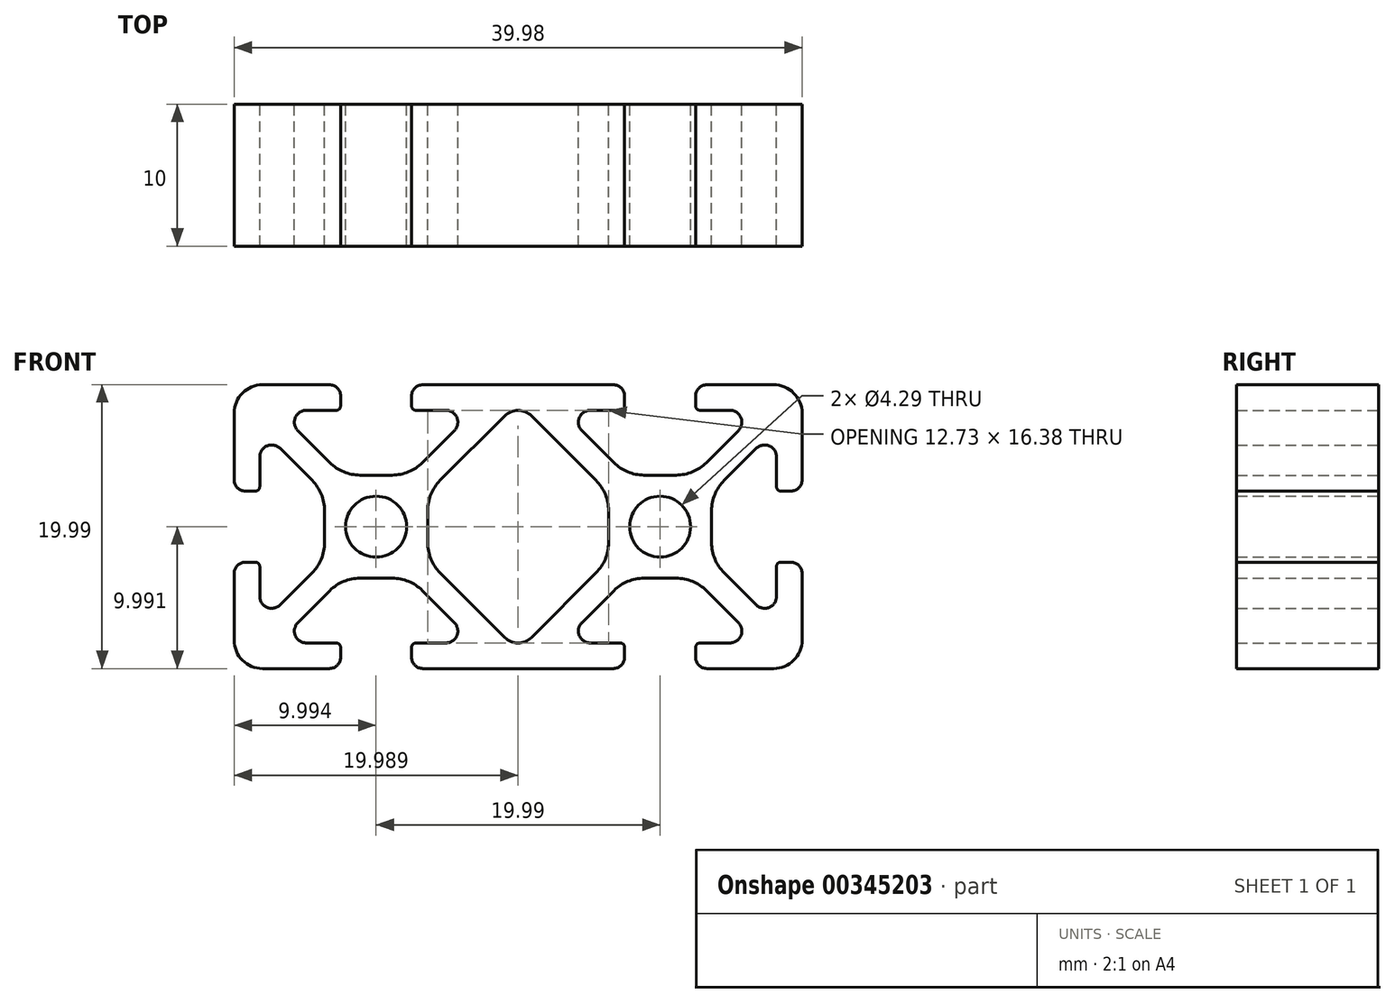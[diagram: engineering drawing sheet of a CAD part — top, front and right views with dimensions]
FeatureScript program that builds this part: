
annotation { "Feature Type Name" : "Feature", "Feature Type Description" : "" }
export const myFeature = defineFeature(function(context is Context, id is Id, definition is map)
    precondition{}
    {
        {
            var Q0;
            Q0=qCreatedBy(makeId("Front.planeOp"),FACE);
            var sketch = newSketch(context, id + "F0", { "sketchPlane" : qUnion([Q0])});
            skArc(sketch, "E0.0.0", {"start": v(-12.02, 4.76) * mm, "mid": v(-13.17, 4.99) * mm, "end": v(-14.14, 5.64) * mm});
            skLineSegment(sketch, "E0.0.1", {"start": v(-14.14, 5.64) * mm, "end": v(-16.4, 7.9) * mm});
            skArc(sketch, "E0.0.2", {"start": v(-16.4, 7.9) * mm, "mid": v(-16.58, 8.8) * mm, "end": v(-15.8, 9.32) * mm});
            skLineSegment(sketch, "E0.0.3", {"start": v(-15.8, 9.32) * mm, "end": v(-13.7, 9.32) * mm});
            skArc(sketch, "E0.0.4", {"start": v(-13.7, 9.32) * mm, "mid": v(-13.48, 9.41) * mm, "end": v(-13.39, 9.63) * mm});
            skLineSegment(sketch, "E0.0.5", {"start": v(-13.39, 9.63) * mm, "end": v(-13.39, 10.34) * mm});
            skArc(sketch, "E0.0.6", {"start": v(-13.39, 10.34) * mm, "mid": v(-13.62, 10.9) * mm, "end": v(-14.18, 11.13) * mm});
            skLineSegment(sketch, "E0.0.7", {"start": v(-14.18, 11.13) * mm, "end": v(-18.87, 11.13) * mm});
            skArc(sketch, "E0.0.8", {"start": v(-18.87, 11.13) * mm, "mid": v(-20.3, 10.54) * mm, "end": v(-20.88, 9.12) * mm});
            skLineSegment(sketch, "E0.0.9", {"start": v(-20.88, 9.12) * mm, "end": v(-20.88, 4.42) * mm});
            skArc(sketch, "E0.0.10", {"start": v(-20.88, 4.42) * mm, "mid": v(-20.65, 3.86) * mm, "end": v(-20.1, 3.63) * mm});
            skLineSegment(sketch, "E0.0.11", {"start": v(-20.1, 3.63) * mm, "end": v(-19.38, 3.63) * mm});
            skArc(sketch, "E0.0.12", {"start": v(-19.38, 3.63) * mm, "mid": v(-19.17, 3.72) * mm, "end": v(-19.08, 3.94) * mm});
            skLineSegment(sketch, "E0.0.13", {"start": v(-19.08, 3.94) * mm, "end": v(-19.08, 6.05) * mm});
            skArc(sketch, "E0.0.14", {"start": v(-19.08, 6.05) * mm, "mid": v(-18.56, 6.82) * mm, "end": v(-17.65, 6.64) * mm});
            skLineSegment(sketch, "E0.0.15", {"start": v(-17.65, 6.64) * mm, "end": v(-15.4, 4.38) * mm});
            skArc(sketch, "E0.0.16", {"start": v(-15.4, 4.38) * mm, "mid": v(-14.74, 3.41) * mm, "end": v(-14.51, 2.26) * mm});
            skLineSegment(sketch, "E0.0.17", {"start": v(-14.51, 2.26) * mm, "end": v(-14.51, 0) * mm});
            skArc(sketch, "E0.0.18", {"start": v(-14.51, 0) * mm, "mid": v(-14.74, -1.15) * mm, "end": v(-15.4, -2.12) * mm});
            skLineSegment(sketch, "E0.0.19", {"start": v(-15.4, -2.12) * mm, "end": v(-17.65, -4.38) * mm});
            skArc(sketch, "E0.0.20", {"start": v(-17.65, -4.38) * mm, "mid": v(-18.56, -4.56) * mm, "end": v(-19.08, -3.78) * mm});
            skLineSegment(sketch, "E0.0.21", {"start": v(-19.08, -3.78) * mm, "end": v(-19.08, -1.68) * mm});
            skArc(sketch, "E0.0.22", {"start": v(-19.08, -1.68) * mm, "mid": v(-19.17, -1.46) * mm, "end": v(-19.38, -1.37) * mm});
            skLineSegment(sketch, "E0.0.23", {"start": v(-19.38, -1.37) * mm, "end": v(-20.1, -1.37) * mm});
            skArc(sketch, "E0.0.24", {"start": v(-20.1, -1.37) * mm, "mid": v(-20.65, -1.6) * mm, "end": v(-20.88, -2.16) * mm});
            skLineSegment(sketch, "E0.0.25", {"start": v(-20.88, -2.16) * mm, "end": v(-20.88, -6.86) * mm});
            skArc(sketch, "E0.0.26", {"start": v(-20.88, -6.86) * mm, "mid": v(-20.3, -8.28) * mm, "end": v(-18.87, -8.86) * mm});
            skLineSegment(sketch, "E0.0.27", {"start": v(-18.87, -8.86) * mm, "end": v(-14.18, -8.86) * mm});
            skArc(sketch, "E0.0.28", {"start": v(-14.18, -8.86) * mm, "mid": v(-13.62, -8.63) * mm, "end": v(-13.39, -8.08) * mm});
            skLineSegment(sketch, "E0.0.29", {"start": v(-13.39, -8.08) * mm, "end": v(-13.39, -7.36) * mm});
            skArc(sketch, "E0.0.30", {"start": v(-13.39, -7.36) * mm, "mid": v(-13.48, -7.15) * mm, "end": v(-13.7, -7.06) * mm});
            skLineSegment(sketch, "E0.0.31", {"start": v(-13.7, -7.06) * mm, "end": v(-15.8, -7.06) * mm});
            skArc(sketch, "E0.0.32", {"start": v(-15.8, -7.06) * mm, "mid": v(-16.58, -6.54) * mm, "end": v(-16.4, -5.63) * mm});
            skLineSegment(sketch, "E0.0.33", {"start": v(-16.4, -5.63) * mm, "end": v(-14.14, -3.37) * mm});
            skArc(sketch, "E0.0.34", {"start": v(-14.14, -3.37) * mm, "mid": v(-13.17, -2.72) * mm, "end": v(-12.02, -2.5) * mm});
            skLineSegment(sketch, "E0.0.35", {"start": v(-12.02, -2.5) * mm, "end": v(-9.75, -2.5) * mm});
            skArc(sketch, "E0.0.36", {"start": v(-9.75, -2.5) * mm, "mid": v(-8.6, -2.72) * mm, "end": v(-7.63, -3.37) * mm});
            skLineSegment(sketch, "E0.0.37", {"start": v(-7.63, -3.37) * mm, "end": v(-5.38, -5.63) * mm});
            skArc(sketch, "E0.0.38", {"start": v(-5.38, -5.63) * mm, "mid": v(-5.2, -6.54) * mm, "end": v(-5.97, -7.06) * mm});
            skLineSegment(sketch, "E0.0.39", {"start": v(-5.97, -7.06) * mm, "end": v(-8.08, -7.06) * mm});
            skArc(sketch, "E0.0.40", {"start": v(-8.08, -7.06) * mm, "mid": v(-8.3, -7.15) * mm, "end": v(-8.38, -7.36) * mm});
            skLineSegment(sketch, "E0.0.41", {"start": v(-8.38, -7.36) * mm, "end": v(-8.38, -8.08) * mm});
            skArc(sketch, "E0.0.42", {"start": v(-8.38, -8.08) * mm, "mid": v(-8.15, -8.63) * mm, "end": v(-7.6, -8.86) * mm});
            skLineSegment(sketch, "E0.0.43", {"start": v(-7.6, -8.86) * mm, "end": v(5.81, -8.86) * mm});
            skArc(sketch, "E0.0.44", {"start": v(5.81, -8.86) * mm, "mid": v(6.37, -8.63) * mm, "end": v(6.6, -8.08) * mm});
            skLineSegment(sketch, "E0.0.45", {"start": v(6.6, -8.08) * mm, "end": v(6.6, -7.36) * mm});
            skArc(sketch, "E0.0.46", {"start": v(6.6, -7.36) * mm, "mid": v(6.51, -7.15) * mm, "end": v(6.3, -7.06) * mm});
            skLineSegment(sketch, "E0.0.47", {"start": v(6.3, -7.06) * mm, "end": v(4.19, -7.06) * mm});
            skArc(sketch, "E0.0.48", {"start": v(4.19, -7.06) * mm, "mid": v(3.41, -6.54) * mm, "end": v(3.6, -5.63) * mm});
            skLineSegment(sketch, "E0.0.49", {"start": v(3.6, -5.63) * mm, "end": v(5.85, -3.37) * mm});
            skArc(sketch, "E0.0.50", {"start": v(5.85, -3.37) * mm, "mid": v(6.82, -2.72) * mm, "end": v(7.97, -2.5) * mm});
            skLineSegment(sketch, "E0.0.51", {"start": v(7.97, -2.5) * mm, "end": v(10.24, -2.5) * mm});
            skArc(sketch, "E0.0.52", {"start": v(10.24, -2.5) * mm, "mid": v(11.38, -2.72) * mm, "end": v(12.36, -3.37) * mm});
            skLineSegment(sketch, "E0.0.53", {"start": v(12.36, -3.37) * mm, "end": v(14.61, -5.63) * mm});
            skArc(sketch, "E0.0.54", {"start": v(14.61, -5.63) * mm, "mid": v(14.8, -6.54) * mm, "end": v(14.02, -7.06) * mm});
            skLineSegment(sketch, "E0.0.55", {"start": v(14.02, -7.06) * mm, "end": v(11.91, -7.06) * mm});
            skArc(sketch, "E0.0.56", {"start": v(11.91, -7.06) * mm, "mid": v(11.7, -7.15) * mm, "end": v(11.6, -7.36) * mm});
            skLineSegment(sketch, "E0.0.57", {"start": v(11.6, -7.36) * mm, "end": v(11.6, -8.08) * mm});
            skArc(sketch, "E0.0.58", {"start": v(11.6, -8.08) * mm, "mid": v(11.84, -8.63) * mm, "end": v(12.4, -8.86) * mm});
            skLineSegment(sketch, "E0.0.59", {"start": v(12.4, -8.86) * mm, "end": v(17.1, -8.86) * mm});
            skArc(sketch, "E0.0.60", {"start": v(17.1, -8.86) * mm, "mid": v(18.51, -8.28) * mm, "end": v(19.1, -6.86) * mm});
            skLineSegment(sketch, "E0.0.61", {"start": v(19.1, -6.86) * mm, "end": v(19.1, -2.16) * mm});
            skArc(sketch, "E0.0.62", {"start": v(19.1, -2.16) * mm, "mid": v(18.87, -1.6) * mm, "end": v(18.31, -1.37) * mm});
            skLineSegment(sketch, "E0.0.63", {"start": v(18.31, -1.37) * mm, "end": v(17.6, -1.37) * mm});
            skArc(sketch, "E0.0.64", {"start": v(17.6, -1.37) * mm, "mid": v(17.38, -1.46) * mm, "end": v(17.3, -1.68) * mm});
            skLineSegment(sketch, "E0.0.65", {"start": v(17.3, -1.68) * mm, "end": v(17.3, -3.78) * mm});
            skArc(sketch, "E0.0.66", {"start": v(17.3, -3.78) * mm, "mid": v(16.78, -4.56) * mm, "end": v(15.86, -4.38) * mm});
            skLineSegment(sketch, "E0.0.67", {"start": v(15.86, -4.38) * mm, "end": v(13.6, -2.12) * mm});
            skArc(sketch, "E0.0.68", {"start": v(13.6, -2.12) * mm, "mid": v(12.96, -1.15) * mm, "end": v(12.73, 0) * mm});
            skLineSegment(sketch, "E0.0.69", {"start": v(12.73, 0) * mm, "end": v(12.73, 2.26) * mm});
            skArc(sketch, "E0.0.70", {"start": v(12.73, 2.26) * mm, "mid": v(12.96, 3.41) * mm, "end": v(13.6, 4.38) * mm});
            skLineSegment(sketch, "E0.0.71", {"start": v(13.6, 4.38) * mm, "end": v(15.86, 6.64) * mm});
            skArc(sketch, "E0.0.72", {"start": v(15.86, 6.64) * mm, "mid": v(16.78, 6.82) * mm, "end": v(17.3, 6.05) * mm});
            skLineSegment(sketch, "E0.0.73", {"start": v(17.3, 6.05) * mm, "end": v(17.3, 3.94) * mm});
            skArc(sketch, "E0.0.74", {"start": v(17.3, 3.94) * mm, "mid": v(17.38, 3.72) * mm, "end": v(17.6, 3.63) * mm});
            skLineSegment(sketch, "E0.0.75", {"start": v(17.6, 3.63) * mm, "end": v(18.31, 3.63) * mm});
            skArc(sketch, "E0.0.76", {"start": v(18.31, 3.63) * mm, "mid": v(18.87, 3.86) * mm, "end": v(19.1, 4.42) * mm});
            skLineSegment(sketch, "E0.0.77", {"start": v(19.1, 4.42) * mm, "end": v(19.1, 9.12) * mm});
            skArc(sketch, "E0.0.78", {"start": v(19.1, 9.12) * mm, "mid": v(18.51, 10.54) * mm, "end": v(17.1, 11.13) * mm});
            skLineSegment(sketch, "E0.0.79", {"start": v(17.1, 11.13) * mm, "end": v(12.4, 11.13) * mm});
            skArc(sketch, "E0.0.80", {"start": v(12.4, 11.13) * mm, "mid": v(11.84, 10.9) * mm, "end": v(11.6, 10.34) * mm});
            skLineSegment(sketch, "E0.0.81", {"start": v(11.6, 10.34) * mm, "end": v(11.6, 9.63) * mm});
            skArc(sketch, "E0.0.82", {"start": v(11.6, 9.63) * mm, "mid": v(11.7, 9.41) * mm, "end": v(11.91, 9.32) * mm});
            skLineSegment(sketch, "E0.0.83", {"start": v(11.91, 9.32) * mm, "end": v(14.02, 9.32) * mm});
            skArc(sketch, "E0.0.84", {"start": v(14.02, 9.32) * mm, "mid": v(14.8, 8.8) * mm, "end": v(14.61, 7.9) * mm});
            skLineSegment(sketch, "E0.0.85", {"start": v(14.61, 7.9) * mm, "end": v(12.36, 5.64) * mm});
            skArc(sketch, "E0.0.86", {"start": v(12.36, 5.64) * mm, "mid": v(11.38, 4.99) * mm, "end": v(10.24, 4.76) * mm});
            skLineSegment(sketch, "E0.0.87", {"start": v(10.24, 4.76) * mm, "end": v(7.97, 4.76) * mm});
            skArc(sketch, "E0.0.88", {"start": v(7.97, 4.76) * mm, "mid": v(6.82, 4.99) * mm, "end": v(5.85, 5.64) * mm});
            skLineSegment(sketch, "E0.0.89", {"start": v(5.85, 5.64) * mm, "end": v(3.6, 7.9) * mm});
            skArc(sketch, "E0.0.90", {"start": v(3.6, 7.9) * mm, "mid": v(3.41, 8.8) * mm, "end": v(4.19, 9.32) * mm});
            skLineSegment(sketch, "E0.0.91", {"start": v(4.19, 9.32) * mm, "end": v(6.3, 9.32) * mm});
            skArc(sketch, "E0.0.92", {"start": v(6.3, 9.32) * mm, "mid": v(6.51, 9.41) * mm, "end": v(6.6, 9.63) * mm});
            skLineSegment(sketch, "E0.0.93", {"start": v(6.6, 9.63) * mm, "end": v(6.6, 10.34) * mm});
            skArc(sketch, "E0.0.94", {"start": v(6.6, 10.34) * mm, "mid": v(6.37, 10.9) * mm, "end": v(5.81, 11.13) * mm});
            skLineSegment(sketch, "E0.0.95", {"start": v(5.81, 11.13) * mm, "end": v(-7.6, 11.13) * mm});
            skArc(sketch, "E0.0.96", {"start": v(-7.6, 11.13) * mm, "mid": v(-8.15, 10.9) * mm, "end": v(-8.38, 10.34) * mm});
            skLineSegment(sketch, "E0.0.97", {"start": v(-8.38, 10.34) * mm, "end": v(-8.38, 9.63) * mm});
            skArc(sketch, "E0.0.98", {"start": v(-8.38, 9.63) * mm, "mid": v(-8.3, 9.41) * mm, "end": v(-8.08, 9.32) * mm});
            skLineSegment(sketch, "E0.0.99", {"start": v(-8.08, 9.32) * mm, "end": v(-5.97, 9.32) * mm});
            skArc(sketch, "E0.0.100", {"start": v(-5.97, 9.32) * mm, "mid": v(-5.2, 8.8) * mm, "end": v(-5.38, 7.9) * mm});
            skLineSegment(sketch, "E0.0.101", {"start": v(-5.38, 7.9) * mm, "end": v(-7.63, 5.64) * mm});
            skArc(sketch, "E0.0.102", {"start": v(-7.63, 5.64) * mm, "mid": v(-8.6, 4.99) * mm, "end": v(-9.75, 4.76) * mm});
            skLineSegment(sketch, "E0.0.103", {"start": v(-9.75, 4.76) * mm, "end": v(-12.02, 4.76) * mm});
            skCircle(sketch, "E1.0", {"center": v(-10.89, 1.13) * mm, "radius": 2.15 * mm});
            skCircle(sketch, "E2.0", {"center": v(9.1, 1.13) * mm, "radius": 2.15 * mm});
            skLineSegment(sketch, "E3.0", {"start": v(-7.26, 2.26) * mm, "end": v(-7.26, 0) * mm});
            skArc(sketch, "E3.1", {"start": v(-6.38, 4.38) * mm, "mid": v(-7.03, 3.41) * mm, "end": v(-7.26, 2.26) * mm});
            skLineSegment(sketch, "E3.2", {"start": v(-1.83, 8.93) * mm, "end": v(-6.38, 4.38) * mm});
            skArc(sketch, "E3.3", {"start": v(-7.26, 0) * mm, "mid": v(-7.03, -1.15) * mm, "end": v(-6.38, -2.12) * mm});
            skLineSegment(sketch, "E3.4", {"start": v(-6.38, -2.12) * mm, "end": v(-1.83, -6.67) * mm});
            skArc(sketch, "E3.5", {"start": v(-1.83, -6.67) * mm, "mid": v(-0.9, -7.06) * mm, "end": v(0.05, -6.67) * mm});
            skLineSegment(sketch, "E3.6", {"start": v(0.05, -6.67) * mm, "end": v(4.6, -2.12) * mm});
            skLineSegment(sketch, "E3.7", {"start": v(4.6, 4.38) * mm, "end": v(0.05, 8.93) * mm});
            skLineSegment(sketch, "E3.8", {"start": v(5.48, 0) * mm, "end": v(5.48, 2.26) * mm});
            skArc(sketch, "E3.9", {"start": v(5.48, 2.26) * mm, "mid": v(5.25, 3.41) * mm, "end": v(4.6, 4.38) * mm});
            skArc(sketch, "E3.10", {"start": v(4.6, -2.12) * mm, "mid": v(5.25, -1.15) * mm, "end": v(5.48, 0) * mm});
            skArc(sketch, "E3.11", {"start": v(0.05, 8.93) * mm, "mid": v(-0.9, 9.32) * mm, "end": v(-1.83, 8.93) * mm});
            skSolve(sketch);
        }
        {
            var Q0;
            Q0=qSketchRegion(id+"F0",true);
            extrude(context, id + "F1", {"entities" : qUnion([Q0]), "depth" : 10 * mm});
        }
    });
